# Revit family: EKF_EE_КомплектМонтажныхПластинДляВертикальныхПерегородок(4 шт)Trivia_AVERES
name_source: partatom
category: Электрооборудование
units: mm (PartAtom-declared; Revit-internal decimal feet)

## family parameters
Всегда вертикально = Нет
На основе рабочей плоскости = Да
Общий = Да
При загрузке вырезать с полостями = Нет
Размер круглого соединителя = Использовать диаметр
Тип детали = Силовой щит
Точка расчета площади = Нет

## types (1)
- Комплект монтажных пластин для вертикальных перегородок (4 шт) EKF AVERES
    ADSK_Единица измерения = шт.
    ADSK_Завод-изготовитель = EKF
    ADSK_Код изделия = PAB4
    ADSK_Количество = 1
    ADSK_Марка = Комплект монтажных пластин для вертикальных перегородок (4 шт) EKF AVERES
    ADSK_Масса = 0
    ADSK_Материал = RAL 7035_Сталь
    ADSK_Наименование = Комплект монтажных пластин для вертикальных перегородок (4 шт) EKF AVERES
    ADSK_Обозначение = Комплект монтажных пластин для вертикальных перегородок (4 шт) EKF AVERES
    ADSK_Размер_Высота = 45 мм
    ADSK_Размер_Глубина = 15 мм
    ADSK_Размер_Ширина = 45 мм
    Глубина = 400 мм
    Изготовитель = EKF
    КоличествоПластинВСтолбце = 2
    Отметка по умолчанию = 1219.2 мм
    Серия номенклатуры = Averes
    Степень защиты IP = -
    ТВ = EKF_2_TRIVIA_AVERES
    Тип = 697 мм
    Тип установки = -
